# Revit family: Silhouette Fan 125B,H,T
name_source: partatom
category: Mechanical Equipment
revit_build: Autodesk Revit 2014 (Build: 20130308_1515(x64)
units: mm (PartAtom-declared; Revit-internal decimal feet)

## types (3) — shared parameters
0V - 10V Proportional Control = Yes
22mm or 32mm Condensate Conection = Yes
AC Frequency Input = 50Hz
AC Voltage Input = 220-240V
App Control = Yes
BMS Connectivity = Yes
Built-In Humidistat = Yes
Country of Manufacture = UK
Depth = 149
Frost Protection = Yes
Height = 187
Manufacturer = Vent-Axia
Operational and Maintenance Manual = http://www.vent-axia.com
SAP Q Approved = Yes
Spigot Depth = 125
Spigot Size = 125
Summer Bypass = Yes
Swtched Live = Yes
URL = www.vent-axia.com
Watts = 20
Width = 187
zero-valued in all types: Part No.

## per-type parameters (varying)
| type | Identity Data | Operating Temperature |
| Silhouette 125B | 445161 | -5C - +40C |
| Silhouette 125T | 445163 |  |
| Silhouette 125H | 445162 |  |

## geometry (parser evidence)
native form markers: Sweep x1
no freeform markers — native parametric forms only
